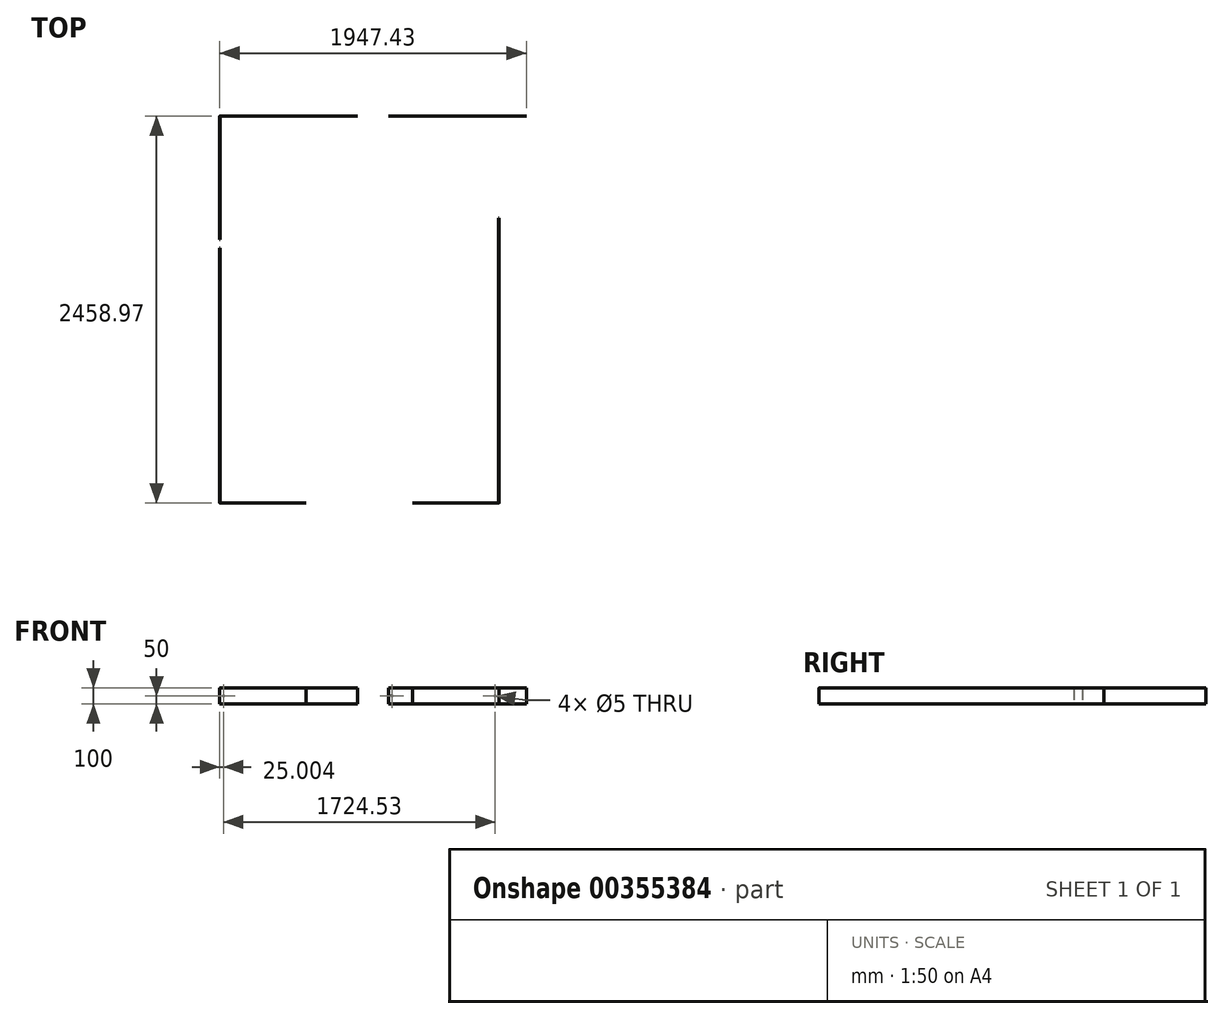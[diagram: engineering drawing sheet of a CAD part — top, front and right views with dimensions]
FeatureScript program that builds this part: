
annotation { "Feature Type Name" : "Feature", "Feature Type Description" : "" }
export const myFeature = defineFeature(function(context is Context, id is Id, definition is map)
    precondition{}
    {
        {
            var Q0;
            Q0=qCreatedBy(makeId("Top.planeOp"),FACE);
            var sketch = newSketch(context, id + "F0", { "sketchPlane" : qUnion([Q0])});
            skLineSegment(sketch, "E0", {"start": v(-339.27, -480.28) * mm, "end": v(-886.27, -480.28) * mm});
            skLineSegment(sketch, "E1", {"start": v(-887.27, -479.28) * mm, "end": v(-887.27, 1137.72) * mm});
            skLineSegment(sketch, "E2", {"start": v(-887.27, 1137.72) * mm, "end": v(-889.27, 1137.72) * mm});
            skLineSegment(sketch, "E3", {"start": v(-889.27, 1137.72) * mm, "end": v(-889.27, -481.28) * mm});
            skLineSegment(sketch, "E4", {"start": v(-888.27, -482.28) * mm, "end": v(-339.27, -482.28) * mm});
            skLineSegment(sketch, "E5", {"start": v(-339.27, -482.28) * mm, "end": v(-339.27, -480.28) * mm});
            skLineSegment(sketch, "E6", {"start": v(335.27, -480.28) * mm, "end": v(882.27, -480.28) * mm});
            skLineSegment(sketch, "E7", {"start": v(883.27, -479.28) * mm, "end": v(883.27, 1327.72) * mm});
            skLineSegment(sketch, "E8", {"start": v(883.27, 1327.72) * mm, "end": v(885.27, 1327.72) * mm});
            skLineSegment(sketch, "E9", {"start": v(335.27, -482.28) * mm, "end": v(335.27, -480.28) * mm});
            skPoint(sketch, "E10.start.orphan", {"position": v(885.27, -482.28) * mm});
            skLineSegment(sketch, "E11", {"start": v(335.27, -482.28) * mm, "end": v(884.27, -482.28) * mm});
            skLineSegment(sketch, "E12", {"start": v(885.27, 1327.72) * mm, "end": v(885.27, -481.28) * mm});
            skLineSegment(sketch, "E13", {"start": v(-889.27, 1191.7) * mm, "end": v(-889.27, 1975.7) * mm});
            skLineSegment(sketch, "E14", {"start": v(-888.27, 1976.7) * mm, "end": v(-14.27, 1976.7) * mm});
            skLineSegment(sketch, "E15", {"start": v(-14.27, 1976.7) * mm, "end": v(-14.27, 1974.7) * mm});
            skLineSegment(sketch, "E16", {"start": v(-14.27, 1974.7) * mm, "end": v(-886.27, 1974.7) * mm});
            skLineSegment(sketch, "E17", {"start": v(-887.27, 1973.7) * mm, "end": v(-887.27, 1191.7) * mm});
            skLineSegment(sketch, "E18", {"start": v(-887.27, 1191.7) * mm, "end": v(-889.27, 1191.7) * mm});
            skPoint(sketch, "E19.visualSharp", {"position": v(-889.27, -482.28) * mm});
            skArc(sketch, "E19.filletArc", {"start": v(-889.27, -481.28) * mm, "mid": v(-888.97, -481.98) * mm, "end": v(-888.27, -482.28) * mm});
            skPoint(sketch, "E20.visualSharp", {"position": v(-887.27, -480.28) * mm});
            skArc(sketch, "E20.filletArc", {"start": v(-887.27, -479.28) * mm, "mid": v(-886.97, -479.98) * mm, "end": v(-886.27, -480.28) * mm});
            skArc(sketch, "E21.filletArc", {"start": v(884.27, -482.28) * mm, "mid": v(884.97, -481.98) * mm, "end": v(885.27, -481.28) * mm});
            skPoint(sketch, "E22.visualSharp", {"position": v(883.27, -480.28) * mm});
            skArc(sketch, "E22.filletArc", {"start": v(882.27, -480.28) * mm, "mid": v(882.97, -479.98) * mm, "end": v(883.27, -479.28) * mm});
            skPoint(sketch, "E23.visualSharp", {"position": v(-887.27, 1974.7) * mm});
            skArc(sketch, "E23.filletArc", {"start": v(-886.27, 1974.7) * mm, "mid": v(-886.97, 1974.4) * mm, "end": v(-887.27, 1973.7) * mm});
            skPoint(sketch, "E24.visualSharp", {"position": v(-889.27, 1976.7) * mm});
            skArc(sketch, "E24.filletArc", {"start": v(-888.27, 1976.7) * mm, "mid": v(-888.97, 1976.4) * mm, "end": v(-889.27, 1975.7) * mm});
            skLineSegment(sketch, "E25", {"start": v(183.16, 1976.7) * mm, "end": v(1058.16, 1976.7) * mm});
            skLineSegment(sketch, "E26", {"start": v(1058.16, 1976.7) * mm, "end": v(1058.16, 1974.7) * mm});
            skLineSegment(sketch, "E27", {"start": v(1058.16, 1974.7) * mm, "end": v(183.16, 1974.7) * mm});
            skLineSegment(sketch, "E28", {"start": v(183.16, 1974.7) * mm, "end": v(183.16, 1976.7) * mm});
            skSolve(sketch);
        }
        {
            var Q0;
            Q0 = qSketchRegion(id + "F0", true);
            extrude(context, id + "F1", {"entities" : qUnion([Q0]), "depth" : 100 * mm, "offsetDistance" : 25 * mm});
        }
        {
            var Q0;
            Q0=makeQuery(id+"F1.opExtrude","SWEPT_FACE",FACE,{"disambiguationData":[OSD([sQuery(id+"F0.wireOp",EDGE,"E14")])]});
            var sketch = newSketch(context, id + "F2", { "sketchPlane" : qUnion([Q0])});
            skLineSegment(sketch, "E29", {"start": v(888.27, 50) * mm, "end": v(864.27, 50) * mm, "construction": true});
            skCircle(sketch, "E30", {"center": v(864.27, 50) * mm, "radius": 2.5 * mm});
            skSolve(sketch);
        }
        {
            var Q0;
            Q0 = qSketchRegion(id + "F2", true);
            extrude(context, id + "F3", {"entities" : qUnion([Q0]), "operationType" : NewBodyOperationType.REMOVE, "oppositeDirection" : true, "depth" : 25 * mm, "offsetDistance" : 25 * mm});
        }
        {
            var Q0;
            Q0=makeQuery(id+"F1.opExtrude","SWEPT_FACE",FACE,{"disambiguationData":[OSD([sQuery(id+"F0.wireOp",EDGE,"E4")])]});
            var sketch = newSketch(context, id + "F4", { "sketchPlane" : qUnion([Q0])});
            skCircle(sketch, "E31", {"center": v(-864.27, 50) * mm, "radius": 2.5 * mm});
            skPoint(sketch, "E32.orphan", {"position": v(-888.27, 50) * mm});
            skSolve(sketch);
        }
        {
            var Q0;
            Q0 = qSketchRegion(id + "F4", true);
            extrude(context, id + "F5", {"entities" : qUnion([Q0]), "operationType" : NewBodyOperationType.REMOVE, "oppositeDirection" : true, "depth" : 25 * mm, "offsetDistance" : 25 * mm});
        }
        {
            var Q0;
            Q0=makeQuery(id+"F1.opExtrude","SWEPT_FACE",FACE,{"disambiguationData":[OSD([sQuery(id+"F0.wireOp",EDGE,"E11")])]});
            var sketch = newSketch(context, id + "F6", { "sketchPlane" : qUnion([Q0])});
            skCircle(sketch, "E33", {"center": v(860.27, 50) * mm, "radius": 2.5 * mm});
            skPoint(sketch, "E34.orphan", {"position": v(884.27, 50) * mm});
            skSolve(sketch);
        }
        {
            var Q0;
            Q0 = qSketchRegion(id + "F6", true);
            extrude(context, id + "F7", {"entities" : qUnion([Q0]), "operationType" : NewBodyOperationType.REMOVE, "oppositeDirection" : true, "depth" : 25 * mm, "offsetDistance" : 25 * mm});
        }
        {
            var Q0;
            Q0=makeQuery(id+"F1.opExtrude","SWEPT_FACE",FACE,{"disambiguationData":[OSD([sQuery(id+"F0.wireOp",EDGE,"E27")])]});
            var sketch = newSketch(context, id + "F8", { "sketchPlane" : qUnion([Q0])});
            skLineSegment(sketch, "E35", {"start": v(1058.16, 50) * mm, "end": v(205.66, 50) * mm, "construction": true});
            skCircle(sketch, "E36", {"center": v(205.66, 50) * mm, "radius": 2.5 * mm});
            skSolve(sketch);
        }
        {
            var Q0;
            Q0 = qSketchRegion(id + "F8", true);
            extrude(context, id + "F9", {"entities" : qUnion([Q0]), "operationType" : NewBodyOperationType.REMOVE, "oppositeDirection" : true, "depth" : 25 * mm, "offsetDistance" : 25 * mm});
        }
    });
